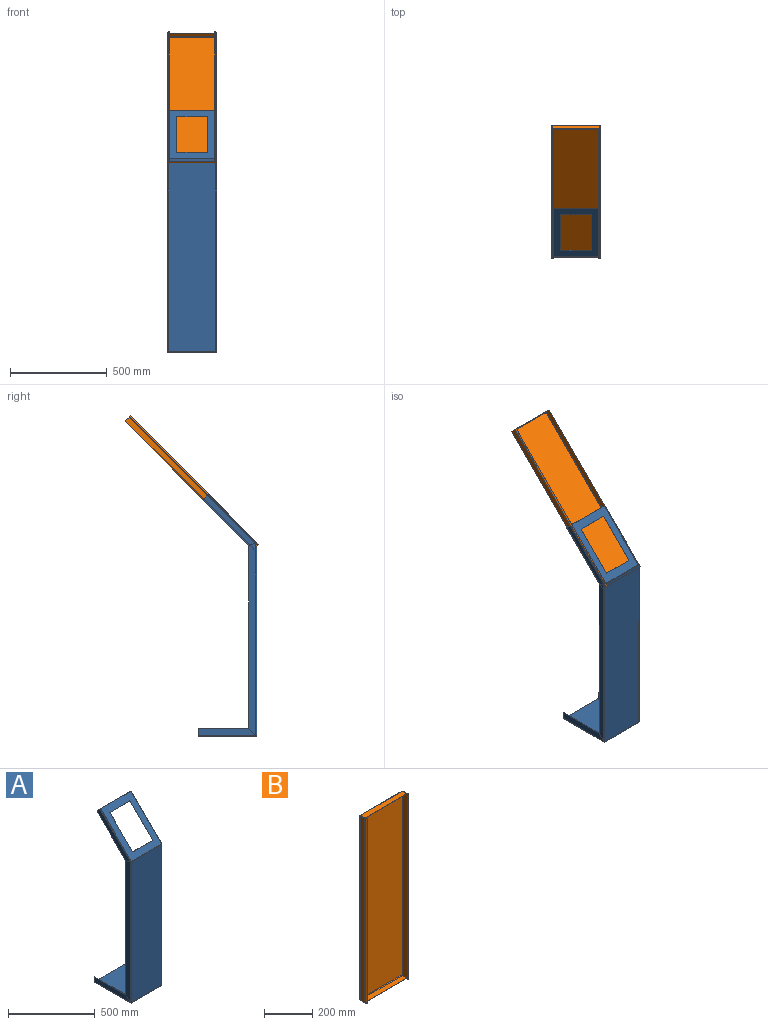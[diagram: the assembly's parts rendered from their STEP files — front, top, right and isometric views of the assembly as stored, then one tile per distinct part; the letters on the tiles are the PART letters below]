
ASSEMBLY  parts=2 mates=1
PART A: 90 faces, bbox 255x300x1251 mm
  f0: plane 1x0.01mm, normal (1,0,0), area 0mm2, adj f4,f5,f68,f87
  f1: plane 1x0.01mm, normal (-1,0,0), area 0mm2, adj f4,f5,f39,f78
  f2: plane 1x0.01mm, normal (1,0,0), area 0mm2, adj f4,f5,f40,f86
  f3: plane 1x0.01mm, normal (-1,0,0), area 0mm2, adj f4,f5,f69,f77
  f4: plane 996.18x247.6mm, normal (0,1,0), area 246654.6mm2, adj f0,f1,f2,f3,f42,f71,f80,f89
  f5: plane 996.18x247.6mm, normal (0,-1,0), area 246654.6mm2, adj f0,f1,f2,f3,f41,f70,f79,f88
  f6: plane 0.71x0.71mm, normal (1,0,0), area 0mm2, adj f13,f14,f25,f40
  f7: plane 182.43x182.43mm, normal (1,0,0), area 257mm2, adj f13,f14,f17,f18
  f8: plane 158x0.71mm, normal (0,0.71,0.71), area 158mm2, adj f13,f14,f16,f17
  f9: plane 182.43x182.43mm, normal (-1,0,0), area 257mm2, adj f13,f14,f15,f16
  f10: plane 247.6x0.71mm, normal (0,0.71,0.71), area 247.6mm2, adj f13,f14,f26,f35
  f11: plane 0.71x0.71mm, normal (-1,0,0), area 0mm2, adj f13,f14,f36,f39
  f12: plane 158x0.71mm, normal (0,-0.71,-0.71), area 158mm2, adj f13,f14,f15,f18
  f13: plane 248.53x248.53mm, normal (0,0.71,-0.71), area 43899.1mm2, adj f6,f7,f8,f9,f10,f11,f12,f15
  f14: plane 248.53x248.53mm, normal (0,-0.71,0.71), area 43899.1mm2, adj f6,f7,f8,f9,f10,f11,f12,f15
  f15: cylinder r=3mm len=3mm, axis (0,-0.71,0.71), area 4.7mm2, adj f9,f12,f13,f14
  f16: cylinder r=3mm len=3mm, axis (0,-0.71,0.71), area 4.7mm2, adj f8,f9,f13,f14
  f17: cylinder r=3mm len=3mm, axis (0,-0.71,0.71), area 4.7mm2, adj f7,f8,f13,f14
  f18: cylinder r=3mm len=3mm, axis (0,-0.71,0.71), area 4.7mm2, adj f7,f12,f13,f14
  f19: plane 234.35x234.35mm, normal (0,0.71,-0.71), area 331.4mm2, adj f20,f22,f23,f24
  f20: plane 36.3x15.04mm, normal (0,-0.38,-0.92), area 39.3mm2, adj f19,f22,f23,f25
  f21: plane 22.13x22.13mm, normal (0,0.71,0.71), area 31.3mm2, adj f22,f23,f24,f26
  f22: plane 272.11x263.55mm, normal (-1,0,0), area 12479.6mm2, adj f19,f20,f21,f24,f28
  f23: plane 272.11x263.55mm, normal (1,0,0), area 12479.6mm2, adj f19,f20,f21,f24,f27
  f24: cylinder r=5mm len=7.07mm, axis (-1,0,0), area 7.9mm2, adj f19,f21,f22,f23
  f25: plane 3.7x2.62mm, normal (0,-0.71,-0.71), area 5mm2, adj f6,f20,f27,f28
  f26: plane 3.7x2.62mm, normal (0,0.71,0.71), area 5mm2, adj f10,f21,f27,f28
  f27: cylinder r=3.7mm len=251.13mm, axis (0,-0.71,-0.71), area 2042.6mm2, adj f14,f23,f25,f26
  f28: cylinder r=2.7mm len=250.43mm, axis (0,-0.71,-0.71), area 1490.6mm2, adj f13,f22,f25,f26
  f29: plane 234.35x234.35mm, normal (0,0.71,-0.71), area 331.4mm2, adj f31,f32,f33,f34
  f30: plane 22.13x22.13mm, normal (0,0.71,0.71), area 31.3mm2, adj f32,f33,f34,f35
  f31: plane 36.3x15.04mm, normal (0,-0.38,-0.92), area 39.3mm2, adj f29,f32,f33,f36
  f32: plane 272.11x263.55mm, normal (1,0,0), area 12479.6mm2, adj f29,f30,f31,f34,f38
  f33: plane 272.11x263.55mm, normal (-1,0,0), area 12479.6mm2, adj f29,f30,f31,f34,f37
  f34: cylinder r=5mm len=7.07mm, axis (1,0,0), area 7.9mm2, adj f29,f30,f32,f33
  f35: plane 3.7x2.62mm, normal (0,0.71,0.71), area 5mm2, adj f10,f30,f37,f38
  f36: plane 3.7x2.62mm, normal (0,-0.71,-0.71), area 5mm2, adj f11,f31,f37,f38
  f37: cylinder r=3.7mm len=251.13mm, axis (0,0.71,0.71), area 2042.6mm2, adj f14,f33,f35,f36
  f38: cylinder r=2.7mm len=250.43mm, axis (0,0.71,0.71), area 1490.6mm2, adj f13,f32,f35,f36
  f39: plane 2.62x1.79mm, normal (-1,0,0), area 2.5mm2, adj f1,f11,f41,f42
  f40: plane 2.62x1.79mm, normal (1,0,0), area 2.5mm2, adj f2,f6,f41,f42
  f41: cylinder r=3.7mm len=247.6mm, axis (-1,0,0), area 719.5mm2, adj f5,f14,f39,f40
  f42: cylinder r=2.7mm len=247.6mm, axis (-1,0,0), area 525.1mm2, adj f4,f13,f39,f40
  f43: plane 1x0.01mm, normal (-1,0,0), area 0mm2, adj f46,f47,f54,f69
  f44: plane 247.6x1mm, normal (0,1,0), area 247.6mm2, adj f46,f47,f55,f64
  f45: plane 1x0.01mm, normal (1,0,0), area 0mm2, adj f46,f47,f65,f68
  f46: plane 296.3x247.6mm, normal (0,0,1), area 73363.9mm2, adj f43,f44,f45,f57,f67,f71
  f47: plane 296.3x247.6mm, normal (0,0,-1), area 73363.9mm2, adj f43,f44,f45,f56,f66,f70
  f48: plane 254.99x1mm, normal (0,0,1), area 255mm2, adj f49,f51,f52,f53
  f49: plane 36.3x36.3mm, normal (0,-0.71,0.71), area 51.3mm2, adj f48,f51,f52,f54
  f50: plane 31.3x1mm, normal (0,1,0), area 31.3mm2, adj f51,f52,f53,f55
  f51: plane 296.29x36.3mm, normal (1,0,0), area 10091mm2, adj f48,f49,f50,f53,f57
  f52: plane 296.29x36.3mm, normal (-1,0,0), area 10091mm2, adj f48,f49,f50,f53,f56
  f53: cylinder r=5mm len=5mm, axis (1,0,0), area 7.9mm2, adj f48,f50,f51,f52
  f54: plane 3.7x3.7mm, normal (0,-1,0), area 5mm2, adj f43,f49,f56,f57
  f55: plane 3.7x3.7mm, normal (0,1,0), area 5mm2, adj f44,f50,f56,f57
  f56: cylinder r=3.7mm len=296.29mm, axis (0,-1,0), area 1722mm2, adj f47,f52,f54,f55
  f57: cylinder r=2.7mm len=296.29mm, axis (0,-1,0), area 1256.6mm2, adj f46,f51,f54,f55
  f58: plane 254.99x1mm, normal (0,0,1), area 255mm2, adj f60,f61,f62,f63
  f59: plane 31.3x1mm, normal (0,1,0), area 31.3mm2, adj f61,f62,f63,f64
  f60: plane 36.3x36.3mm, normal (0,-0.71,0.71), area 51.3mm2, adj f58,f61,f62,f65
  f61: plane 296.29x36.3mm, normal (-1,0,0), area 10091mm2, adj f58,f59,f60,f63,f67
  f62: plane 296.29x36.3mm, normal (1,0,0), area 10091mm2, adj f58,f59,f60,f63,f66
  f63: cylinder r=5mm len=5mm, axis (-1,0,0), area 7.9mm2, adj f58,f59,f61,f62
  f64: plane 3.7x3.7mm, normal (0,1,0), area 5mm2, adj f44,f59,f66,f67
  f65: plane 3.7x3.7mm, normal (0,-1,0), area 5mm2, adj f45,f60,f66,f67
  f66: cylinder r=3.7mm len=296.29mm, axis (0,1,0), area 1722mm2, adj f47,f62,f64,f65
  f67: cylinder r=2.7mm len=296.29mm, axis (0,1,0), area 1256.6mm2, adj f46,f61,f64,f65
  f68: plane 3.7x3.7mm, normal (1,0,0), area 5mm2, adj f0,f45,f70,f71
  f69: plane 3.7x3.7mm, normal (-1,0,0), area 5mm2, adj f3,f43,f70,f71
  f70: cylinder r=3.7mm len=247.6mm, axis (1,0,0), area 1439mm2, adj f5,f47,f68,f69
  f71: cylinder r=2.7mm len=247.6mm, axis (1,0,0), area 1050.1mm2, adj f4,f46,f68,f69
  f72: plane 944.82x1mm, normal (0,1,0), area 944.8mm2, adj f73,f74,f75,f76
  f73: plane 36.3x15.04mm, normal (0,0.38,0.92), area 39.3mm2, adj f72,f75,f76,f78
  f74: plane 36.3x36.3mm, normal (0,0.71,-0.71), area 51.3mm2, adj f72,f75,f76,f77
  f75: plane 996.16x36.3mm, normal (1,0,0), area 35228.7mm2, adj f72,f73,f74,f80
  f76: plane 996.16x36.3mm, normal (-1,0,0), area 35228.7mm2, adj f72,f73,f74,f79
  f77: plane 3.7x3.7mm, normal (0,0,-1), area 5mm2, adj f3,f74,f79,f80
  f78: plane 3.7x3.7mm, normal (0,0,1), area 5mm2, adj f1,f73,f79,f80
  f79: cylinder r=3.7mm len=996.16mm, axis (0,0,-1), area 5789.6mm2, adj f5,f76,f77,f78
  f80: cylinder r=2.7mm len=996.16mm, axis (0,0,-1), area 4224.8mm2, adj f4,f75,f77,f78
  f81: plane 944.82x1mm, normal (0,1,0), area 944.8mm2, adj f82,f83,f84,f85
  f82: plane 36.3x36.3mm, normal (0,0.71,-0.71), area 51.3mm2, adj f81,f84,f85,f87
  f83: plane 36.3x15.04mm, normal (0,0.38,0.92), area 39.3mm2, adj f81,f84,f85,f86
  f84: plane 996.16x36.3mm, normal (-1,0,0), area 35228.7mm2, adj f81,f82,f83,f89
  f85: plane 996.16x36.3mm, normal (1,0,0), area 35228.7mm2, adj f81,f82,f83,f88
  f86: plane 3.7x3.7mm, normal (0,0,1), area 5mm2, adj f2,f83,f88,f89
  f87: plane 3.7x3.7mm, normal (0,0,-1), area 5mm2, adj f0,f82,f88,f89
  f88: cylinder r=3.7mm len=996.16mm, axis (0,0,1), area 5789.6mm2, adj f5,f85,f86,f87
  f89: cylinder r=2.7mm len=996.16mm, axis (0,0,1), area 4224.8mm2, adj f4,f84,f86,f87
PART B: 58 faces, bbox 253x41x940 mm
  f0: plane 245.6x1mm, normal (0,-1,0), area 245.6mm2, adj f1,f2,f3,f4
  f1: plane 26.3x1mm, normal (1,0,0), area 26.3mm2, adj f0,f3,f4,f5
  f2: plane 26.3x1mm, normal (-1,0,0), area 26.3mm2, adj f0,f3,f4,f6
  f3: plane 245.6x26.3mm, normal (0,0,1), area 6459.3mm2, adj f0,f1,f2,f7
  f4: plane 245.6x26.3mm, normal (0,0,-1), area 6459.3mm2, adj f0,f1,f2,f8
  f5: plane 3.7x3.7mm, normal (1,0,0), area 5mm2, adj f1,f7,f8,f46
  f6: plane 3.7x3.7mm, normal (-1,0,0), area 5mm2, adj f2,f7,f8,f27
  f7: cylinder r=3.7mm len=245.6mm, axis (1,0,0), area 1427.4mm2, adj f3,f5,f6,f9
  f8: cylinder r=2.7mm len=245.6mm, axis (1,0,0), area 1041.6mm2, adj f4,f5,f6,f10
  f9: plane 932.6x245.6mm, normal (0,1,0), area 229046.6mm2, adj f7,f18,f28,f47
  f10: plane 932.6x245.6mm, normal (0,-1,0), area 229046.6mm2, adj f8,f19,f29,f48
  f11: plane 245.6x1mm, normal (0,-1,0), area 245.6mm2, adj f12,f13,f14,f15
  f12: plane 26.3x1mm, normal (-1,0,0), area 26.3mm2, adj f11,f14,f15,f16
  f13: plane 26.3x1mm, normal (1,0,0), area 26.3mm2, adj f11,f14,f15,f17
  f14: plane 245.6x26.3mm, normal (0,0,-1), area 6459.3mm2, adj f11,f12,f13,f18
  f15: plane 245.6x26.3mm, normal (0,0,1), area 6459.3mm2, adj f11,f12,f13,f19
  f16: plane 3.7x3.7mm, normal (-1,0,0), area 5mm2, adj f12,f18,f19,f26
  f17: plane 3.7x3.7mm, normal (1,0,0), area 5mm2, adj f13,f18,f19,f45
  f18: cylinder r=3.7mm len=245.6mm, axis (-1,0,0), area 1427.4mm2, adj f9,f14,f16,f17
  f19: cylinder r=2.7mm len=245.6mm, axis (-1,0,0), area 1041.6mm2, adj f10,f15,f16,f17
  f20: plane 2.7x1mm, normal (0,1,0), area 2.7mm2, adj f21,f24,f25,f27
  f21: plane 28.69x1mm, normal (0,0,1), area 28.7mm2, adj f20,f24,f25,f31
  f22: plane 2.7x1mm, normal (0,1,0), area 2.7mm2, adj f23,f24,f25,f26
  f23: plane 28.69x1mm, normal (0,0,-1), area 28.7mm2, adj f22,f24,f25,f30
  f24: plane 938x28.69mm, normal (-1,0,0), area 26912.7mm2, adj f20,f21,f22,f23,f28,f32
  f25: plane 938x28.69mm, normal (1,0,0), area 26912.7mm2, adj f20,f21,f22,f23,f29,f33
  f26: plane 3.7x3.7mm, normal (0,0,-1), area 5mm2, adj f16,f22,f28,f29
  f27: plane 3.7x3.7mm, normal (0,0,1), area 5mm2, adj f6,f20,f28,f29
  f28: cylinder r=3.7mm len=932.6mm, axis (0,0,-1), area 5420.2mm2, adj f9,f24,f26,f27
  f29: cylinder r=2.7mm len=932.6mm, axis (0,0,-1), area 3955.3mm2, adj f10,f25,f26,f27
  f30: plane 2.62x1.79mm, normal (0,0,-1), area 2.5mm2, adj f23,f32,f33,f36
  f31: plane 2.62x1.79mm, normal (0,0,1), area 2.5mm2, adj f21,f32,f33,f35
  f32: cylinder r=3.7mm len=938mm, axis (0,0,-1), area 2725.8mm2, adj f24,f30,f31,f37
  f33: cylinder r=2.7mm len=938mm, axis (0,0,-1), area 1989.1mm2, adj f25,f30,f31,f38
  f34: plane 938x0.71mm, normal (0.71,-0.71,0), area 938mm2, adj f35,f36,f37,f38
  f35: plane 6.69x6.69mm, normal (0,0,1), area 8.5mm2, adj f31,f34,f37,f38
  f36: plane 6.69x6.69mm, normal (0,0,-1), area 8.5mm2, adj f30,f34,f37,f38
  f37: plane 938x5.99mm, normal (-0.71,-0.71,0), area 7942.4mm2, adj f32,f34,f35,f36
  f38: plane 938x5.99mm, normal (0.71,0.71,0), area 7942.4mm2, adj f33,f34,f35,f36
  f39: plane 2.7x1mm, normal (0,1,0), area 2.7mm2, adj f40,f43,f44,f45
  f40: plane 28.69x1mm, normal (0,0,-1), area 28.7mm2, adj f39,f43,f44,f50
  f41: plane 2.7x1mm, normal (0,1,0), area 2.7mm2, adj f42,f43,f44,f46
  f42: plane 28.69x1mm, normal (0,0,1), area 28.7mm2, adj f41,f43,f44,f49
  f43: plane 938x28.69mm, normal (1,0,0), area 26912.7mm2, adj f39,f40,f41,f42,f47,f51
  f44: plane 938x28.69mm, normal (-1,0,0), area 26912.7mm2, adj f39,f40,f41,f42,f48,f52
  f45: plane 3.7x3.7mm, normal (0,0,-1), area 5mm2, adj f17,f39,f47,f48
  f46: plane 3.7x3.7mm, normal (0,0,1), area 5mm2, adj f5,f41,f47,f48
  f47: cylinder r=3.7mm len=932.6mm, axis (0,0,-1), area 5420.2mm2, adj f9,f43,f45,f46
  f48: cylinder r=2.7mm len=932.6mm, axis (0,0,-1), area 3955.3mm2, adj f10,f44,f45,f46
  f49: plane 2.62x1.79mm, normal (0,0,1), area 2.5mm2, adj f42,f51,f52,f55
  f50: plane 2.62x1.79mm, normal (0,0,-1), area 2.5mm2, adj f40,f51,f52,f54
  f51: cylinder r=3.7mm len=938mm, axis (0,0,1), area 2725.8mm2, adj f43,f49,f50,f56
  f52: cylinder r=2.7mm len=938mm, axis (0,0,1), area 1989.1mm2, adj f44,f49,f50,f57
  f53: plane 938x0.71mm, normal (-0.71,-0.71,0), area 938mm2, adj f54,f55,f56,f57
  f54: plane 6.69x6.69mm, normal (0,0,-1), area 8.5mm2, adj f50,f53,f56,f57
  f55: plane 6.69x6.69mm, normal (0,0,1), area 8.5mm2, adj f49,f53,f56,f57
  f56: plane 938x5.99mm, normal (0.71,-0.71,0), area 7942.4mm2, adj f51,f53,f54,f55
  f57: plane 938x5.99mm, normal (-0.71,0.71,0), area 7942.4mm2, adj f52,f53,f54,f55
PLACE A t=(-586.27,44.66,-393.12)mm
PLACE B rot(axis=(-1,0,0),45deg) t=(-436.22,180.7,690.6)mm
MATE planar B.f24 <-> A.f32  axis (-1,0,0) through (-586.27,379.96,915.38)mm
